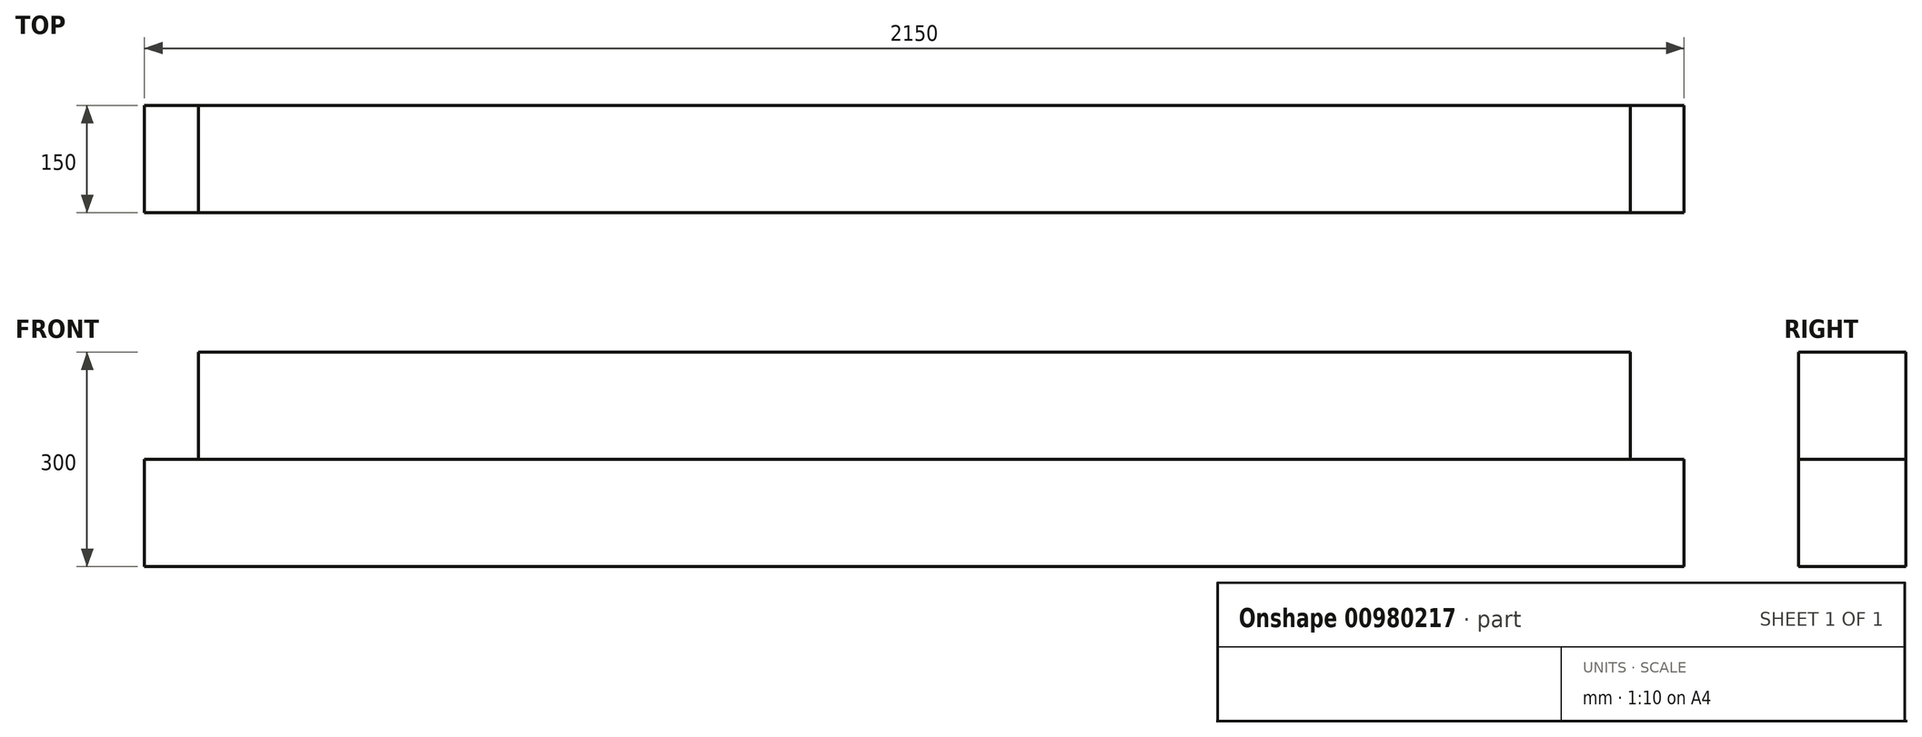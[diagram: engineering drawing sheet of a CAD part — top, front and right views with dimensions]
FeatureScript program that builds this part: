
annotation { "Feature Type Name" : "Feature", "Feature Type Description" : "" }
export const myFeature = defineFeature(function(context is Context, id is Id, definition is map)
    precondition{}
    {
        {
            var Q0;
            Q0=qCreatedBy(makeId("Right.planeOp"),FACE);
            var sketch = newSketch(context, id + "F0", { "sketchPlane" : qUnion([Q0])});
            skLineSegment(sketch, "E0.bottom", {"start": v(75, -75) * mm, "end": v(-75, -75) * mm});
            skLineSegment(sketch, "E0.top", {"start": v(75, 75) * mm, "end": v(-75, 75) * mm});
            skLineSegment(sketch, "E0.left", {"start": v(75, -75) * mm, "end": v(75, 75) * mm});
            skLineSegment(sketch, "E0.right", {"start": v(-75, -75) * mm, "end": v(-75, 75) * mm});
            skPoint(sketch, "E0.middle", {"position": v(0, 0) * mm});
            skLineSegment(sketch, "E1", {"start": v(75, 75) * mm, "end": v(75, 225) * mm});
            skLineSegment(sketch, "E2", {"start": v(75, 225) * mm, "end": v(-75, 225) * mm});
            skLineSegment(sketch, "E3", {"start": v(-75, 225) * mm, "end": v(-75, 75) * mm});
            skSolve(sketch);
        }
        {
            var Q0;
            Q0=makeQuery(id+"F0.imprint","IMPRINT",FACE,{"disambiguationData":[TD([[makeQuery(id+"F0.imprint","IMPRINT",EDGE,{"derivedFrom":sQuery(id+"F0.wireOp",EDGE,"E0.bottom")}),-1.0]])]});
            extrude(context, id + "F1", {"entities" : qUnion([Q0]), "endBound" : BoundingType.SYMMETRIC, "depth" : 2150 * mm, "offsetDistance" : 25 * mm});
        }
        {
            var Q0;
            Q0=makeQuery(id+"F0.imprint","IMPRINT",FACE,{"disambiguationData":[TD([[makeQuery(id+"F0.imprint","IMPRINT",EDGE,{"derivedFrom":sQuery(id+"F0.wireOp",EDGE,"E0.top")}),-1.0]])]});
            extrude(context, id + "F2", {"entities" : qUnion([Q0]), "endBound" : BoundingType.SYMMETRIC, "depth" : 2000 * mm, "offsetDistance" : 25 * mm});
        }
    });
